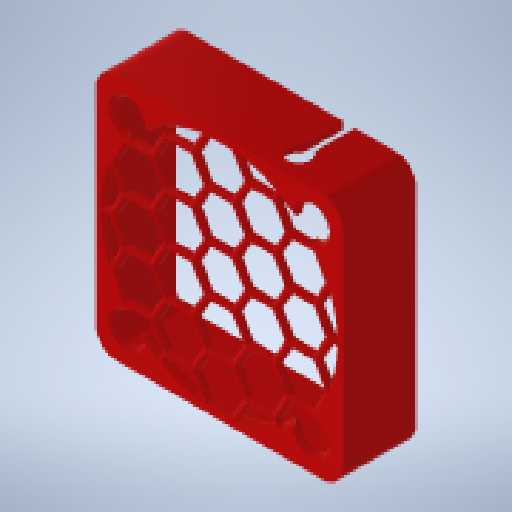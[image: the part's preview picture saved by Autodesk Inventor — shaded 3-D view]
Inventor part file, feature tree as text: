
AUTODESK INVENTOR PART (.ipt)
format: ipt  version: 2023.1 (Build 271208000, 208)  size: 1,460,224 bytes
history: native  units: mm
features: reference x30, sketch x14, extrude x13, chamfer x12, projected_geometry x7, other x6, fillet x3, plane x2, mirror x2, delete_face x2, hole x2
ambient origin geometry x8: Origin, YZ Plane, XZ Plane, XY Plane, X Axis, Y Axis, Z Axis, Center Point
bodies: Volumenkörper1 (feature_tree)
feature tree (93):
  extrude  "Extrusion1"  Depth=0.3mm
  extrude  "Extrusion2"  Depth=0.3mm
  chamfer  "Fase1"  Distance=11.8mm
  chamfer  "Fase2"  Distance=1.0mm
  extrude  "Extrusion3"  Depth=2.0mm TaperAngle=45.0deg
  plane  "Arbeitsebene1"
  plane  "Arbeitsebene2"
  mirror  "Spiegeln1"
  mirror  "Spiegeln2"
  extrude  "Extrusion6"  Depth=2.0mm TaperAngle=45.0deg
  chamfer  "Fase3"  Distance=0.4mm
  delete_face  "Fläche löschen5"
  chamfer  "Fase4"  [1 undecoded]
  chamfer  "Fase5"  Distance=7.0mm
  extrude  "Extrusion7"  Depth=10.0mm
  fillet  "Rundung1"  Radius=1.2mm
  extrude  "Extrusion8"  Depth=1.2mm
  extrude  "Extrusion9"  Depth=1.2mm
  extrude  "Extrusion10"  Depth=1.2mm
  sketch  "Skizze11"  dims[d14=5.2mm]
  hole  "Bohrung1"  [1 undecoded]
  chamfer  "Fase6"  Distance=1.2mm
  extrude  "Extrusion11"  Depth=1.2mm
  chamfer  "Fase8"  Distance=1.2mm
  chamfer  "Fase9"  Distance=1.2mm
  delete_face  "Fläche löschen6"
  extrude  "Extrusion12"  Depth=1.2mm
  chamfer  "Fase10"  Distance=7.0mm
  extrude  "Extrusion13"  Depth=10.0mm
  chamfer  "Fase11"  Distance=7.0mm
  extrude  "Extrusion14"  Depth=10.0mm
  hole  "Bohrung2"  [1 undecoded]
  chamfer  "Fase12"  Distance=7.0mm
  fillet  "Rundung2"  Radius=7.0mm
  chamfer  "Fase13"  Distance=7.0mm
  fillet  "Rundung3"  Radius=1.2mm
  extrude  "Extrusion15"  Depth=1.2mm
  sketch  "Skizze1"  dims[d0=0.3mm d1=0.3mm]
  reference  "Referenz1"
  reference  "Referenz2"
  reference  "Referenz3"
  reference  "Referenz4"
  reference  "Referenz5"
  reference  "Referenz6"
  reference  "Referenz7"
  reference  "Referenz8"
  reference  "Referenz9"
  reference  "Referenz10"
  reference  "Referenz11"
  reference  "Referenz12"
  reference  "Referenz13"
  reference  "Referenz14"
  reference  "Referenz15"
  reference  "Referenz16"
  reference  "Referenz17"
  sketch  "Skizze2"  dims[d2=0.3mm d3=0.3mm]
  projected_geometry  "Projizierte Kontur1"
  reference  "Referenz18"
  reference  "Referenz19"
  reference  "Referenz20"
  reference  "Referenz21"
  reference  "Referenz22"
  sketch  "Skizze3"  dims[d5=0.3mm]
  sketch  "Skizze4"  dims[d6=1.2mm]
  reference  "Referenz23"
  sketch  "Skizze7"  dims[d7=1.2mm]
  reference  "Referenz24"
  reference  "Referenz25"
  sketch  "Skizze8"  dims[d8=1.2mm]
  reference  "Referenz26"
  projected_geometry  "Projizierte Kontur2"
  sketch  "Skizze9"  dims[d9=1.2mm]
  projected_geometry  "Projizierte Kontur3"
  sketch  "Skizze10"  dims[d11=1.2mm d12=11.8mm d13=0.0mm]
  projected_geometry  "Projizierte Kontur4"
  reference  "Referenz27"
  reference  "Referenz28"
  reference  "Referenz29"
  reference  "Referenz30"
  sketch  "Skizze12"  dims[d15=5.2mm]
  projected_geometry  "Projizierte Kontur5"
  sketch  "Skizze13"  dims[d16=5.2mm]
  projected_geometry  "Projizierte Kontur6"
  sketch  "Skizze14"  dims[d17=5.2mm]
  sketch  "Skizze15"  dims[d19=40.0mm]
  sketch  "Skizze16"  dims[d20=0.120048mm d21=1.0mm d22=0.0mm d23=0.6mm d24=2.0mm d25=45.0deg d26=0.6mm d27=2.0mm d28=45.0deg d29=0.4mm d30=0.0mm d31=0.0mm d32=7.0mm d33=7.0mm d34=7.0mm d35=1.2mm d36=7.0mm d37=7.0mm d38=1.2mm d39=7.0mm d40=7.0mm d41=1.2mm d42=1.2mm d43=1.2mm d44=1.2mm d45=7.0mm d46=7.0mm d47=1.2mm d48=7.0mm d49=7.0mm d50=1.2mm d51=1.2mm d52=1.2mm d53=1.2mm d54=7.0mm d55=1.2mm d56=1.2mm d57=1.2mm d58=1.2mm d59=7.0mm d60=7.0mm d61=1.2mm d62=7.0mm d63=7.0mm d64=1.2mm d65=1.2mm d66=1.2mm d67=1.2mm d68=7.0mm d69=7.0mm d70=1.2mm d71=7.0mm d72=7.0mm d73=1.2mm d74=1.2mm d75=1.2mm d76=1.2mm d77=1.2mm d78=1.2mm d79=1.2mm d80=7.0mm d81=1.2mm d82=7.0mm d104=7.0mm d105=1.2mm d106=7.0mm d107=1.2mm d108=1.2mm d109=1.2mm d111=7.0mm d113=7.0mm d114=7.0mm d115=7.0mm d116=7.0mm d117=7.0mm d118=7.0mm d119=7.0mm d120=7.0mm d121=7.0mm d122=7.0mm d123=7.0mm d124=7.0mm d125=7.0mm d126=1.2mm d127=1.2mm d128=1.2mm d129=1.2mm d131=1.2mm d132=1.2mm d133=1.2mm d134=1.2mm d135=1.2mm d136=1.2mm d137=1.2mm d138=1.2mm d139=1.2mm d140=1.2mm d141=1.2mm d142=1.2mm d143=7.0mm d144=7.0mm d145=1.2mm d146=1.2mm d147=1.2mm d148=1.2mm d151=7.0mm d152=7.0mm d153=7.0mm d154=7.0mm d155=7.0mm d156=7.0mm d157=7.0mm d158=7.0mm d159=7.0mm d162=1.2mm d163=1.2mm d164=1.2mm d165=1.2mm d166=1.2mm d167=7.0mm d168=1.2mm d169=1.2mm d170=7.0mm d171=1.2mm d173=1.2mm d174=1.2mm d175=1.2mm d176=1.2mm d177=7.0mm d178=7.0mm d179=7.0mm d180=7.0mm d181=7.0mm d182=1.2mm d183=1.2mm d184=1.2mm d185=1.2mm d186=1.2mm d187=1.2mm d188=1.2mm d189=1.2mm d190=1.2mm d191=41.2mm d206=1.0mm d207=0.0mm d208=0.4mm d209=2.0mm d210=45.0deg d211=0.4mm d212=2.0mm d213=45.0deg d214=0.4mm d215=2.0mm d216=45.0deg d217=0.889mm d218=2.0mm d219=0.5555mm d220=0.5555mm d221=4.0mm d222=0.0mm d223=1.333333mm d224=4.0mm d225=10.0mm d226=0.0mm d227=1.0mm d228=6.4mm d229=1.2mm d230=1.2mm d231=1.2mm d232=1.2mm d233=4.0mm d234=3.6mm d235=2.4mm d236=10.0mm d237=0.0mm d238=2.0mm d239=0.0mm d240=1.2mm d241=3.0mm d242=4.2mm d244=5.0mm d245=5.0mm d246=3.8mm d247=1.2mm d248=1.2mm d249=3.0mm d250=4.2mm d251=5.6mm d252=1.6mm d253=1.2mm d254=4.2mm d255=3.0mm d256=1.0mm d257=1.2mm d258=10.0mm d259=0.0mm d260=3.4mm d261=6.0mm d262=5.6mm d263=5.0mm d264=90.0deg d265=8.0mm d266=20.594885mm d267=0.55mm d268=2.0mm d269=45.0deg d270=2.0mm d271=0.0mm d275=1.0mm d276=2.0mm d277=45.0deg d278=0.4mm d279=2.0mm d280=45.0deg d281=1.0mm d282=1.0mm d283=1.0mm d284=1.0mm d286=1.0mm d287=1.0mm d289=1.0mm d291=1.0mm d292=0.2mm d293=0.0mm d294=1.0mm d295=2.0mm d296=45.0deg d297=2.0mm d298=15.0mm d299=1.2mm d300=0.0mm d301=1.0mm d302=2.0mm d303=45.0deg d304=6.4mm d305=6.4mm d306=1.2mm d307=0.0mm d308=1.2mm d309=0.0mm d310=3.4mm d311=6.0mm d312=5.6mm d313=5.0mm d314=90.0deg d315=8.0mm d316=20.594885mm d317=0.4mm d318=2.0mm d319=45.0deg d320=3.0mm d321=0.55mm d322=2.0mm d323=45.0deg d324=3.0mm d328=1.2mm d329=1.2mm d330=1.2mm d333=1.2mm d334=10.0mm d335=0.0mm]
  projected_geometry  "Projizierte Kontur7"
  other  "<userpath>\Desktop\GitHub\Voron-2-Mods\Arducam_IMX477_CM4\CM4\CAD\CM4_Case.iam"
  other  "CM4_Case.iam"
  other  "Noctua-Fan-NF-A4x10_40mm:1"
  other  "Noctua-NF-A4x10 v1:1"
  other  "Noctua nf-a8-pwm fan 40x40x10 v2:1"
  other  "CM4_Case_Top:1"
note: 3 required parameter values undecoded (feature->parameter linkage not recoverable at this tier; creation-order binding heuristic only, values carry confidence <= 0.55)
